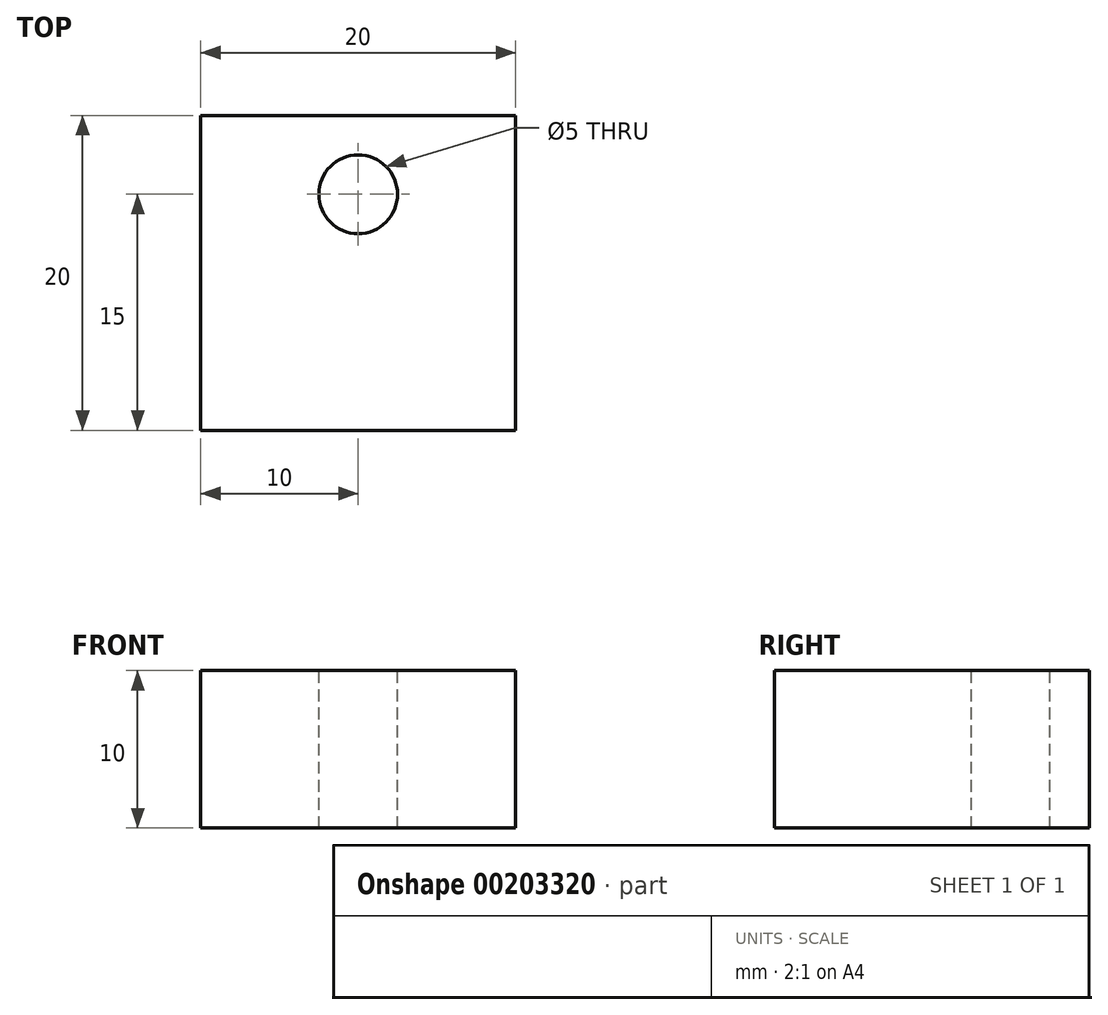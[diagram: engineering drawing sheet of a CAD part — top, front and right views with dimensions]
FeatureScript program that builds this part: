
annotation { "Feature Type Name" : "Feature", "Feature Type Description" : "" }
export const myFeature = defineFeature(function(context is Context, id is Id, definition is map)
    precondition{}
    {
        {
            var Q0;
            Q0=qCreatedBy(makeId("Top.planeOp"),FACE);
            var sketch = newSketch(context, id + "F0", { "sketchPlane" : qUnion([Q0])});
            skLineSegment(sketch, "E0.bottom", {"start": v(10, -10) * mm, "end": v(-10, -10) * mm});
            skLineSegment(sketch, "E0.top", {"start": v(10, 10) * mm, "end": v(-10, 10) * mm});
            skLineSegment(sketch, "E0.left", {"start": v(10, -10) * mm, "end": v(10, 10) * mm});
            skLineSegment(sketch, "E0.right", {"start": v(-10, -10) * mm, "end": v(-10, 10) * mm});
            skPoint(sketch, "E0.middle", {"position": v(0, 0) * mm});
            skSolve(sketch);
        }
        {
            var Q0;
            Q0 = qSketchRegion(id + "F0", true);
            extrude(context, id + "F1", {"entities" : qUnion([Q0]), "depth" : 10 * mm});
        }
        {
            var Q0;
            Q0=makeQuery(id+"F1.opExtrude","CAP_FACE",FACE,{"disambiguationData":[OSD([sQuery(id+"F0.wireOp",EDGE,"E0.bottom"),sQuery(id+"F0.wireOp",EDGE,"E0.top"),sQuery(id+"F0.wireOp",EDGE,"E0.left"),sQuery(id+"F0.wireOp",EDGE,"E0.right")])],"isStart":false});
            var sketch = newSketch(context, id + "F2", { "sketchPlane" : qUnion([Q0])});
            skPoint(sketch, "E1", {"position": v(0, 5) * mm});
            skPoint(sketch, "E1.positionSnap0", {"position": v(0, 10) * mm});
            skSolve(sketch);
        }
        {
            var Q0;
            Q0=sQuery(id+"F2.wireOp",VERTEX,"E1");
            var Q1;
            Q1=makeQuery(id+"F1.opExtrude","SWEPT_BODY",BODY,{"disambiguationData":[OSD([sQuery(id+"F0.wireOp",EDGE,"E0.bottom"),sQuery(id+"F0.wireOp",EDGE,"E0.top"),sQuery(id+"F0.wireOp",EDGE,"E0.left"),sQuery(id+"F0.wireOp",EDGE,"E0.right")])]});
            hole(context, id + "F3", {"style" : HoleStyle.SIMPLE, "endStyle" : HoleEndStyle.BLIND, "standardTappedOrClearance" : lookupTablePath({ "standard" : "ISO", "engagement" : "75%", "pitch" : "1 mm", "size" : "M6", "type" : "Tapped" }), "standardBlindInLast" : lookupTablePath({ "standard" : "ISO", "engagement" : "75%", "pitch" : "1 mm", "size" : "M6", "type" : "Tapped" }), "holeDiameter" : 5 * mm, "holeDepth" : 10 * mm, "locations" : qUnion([Q0]), "scope" : qUnion([Q1]), "majorDiameter" : 6 * mm});
        }
    });
